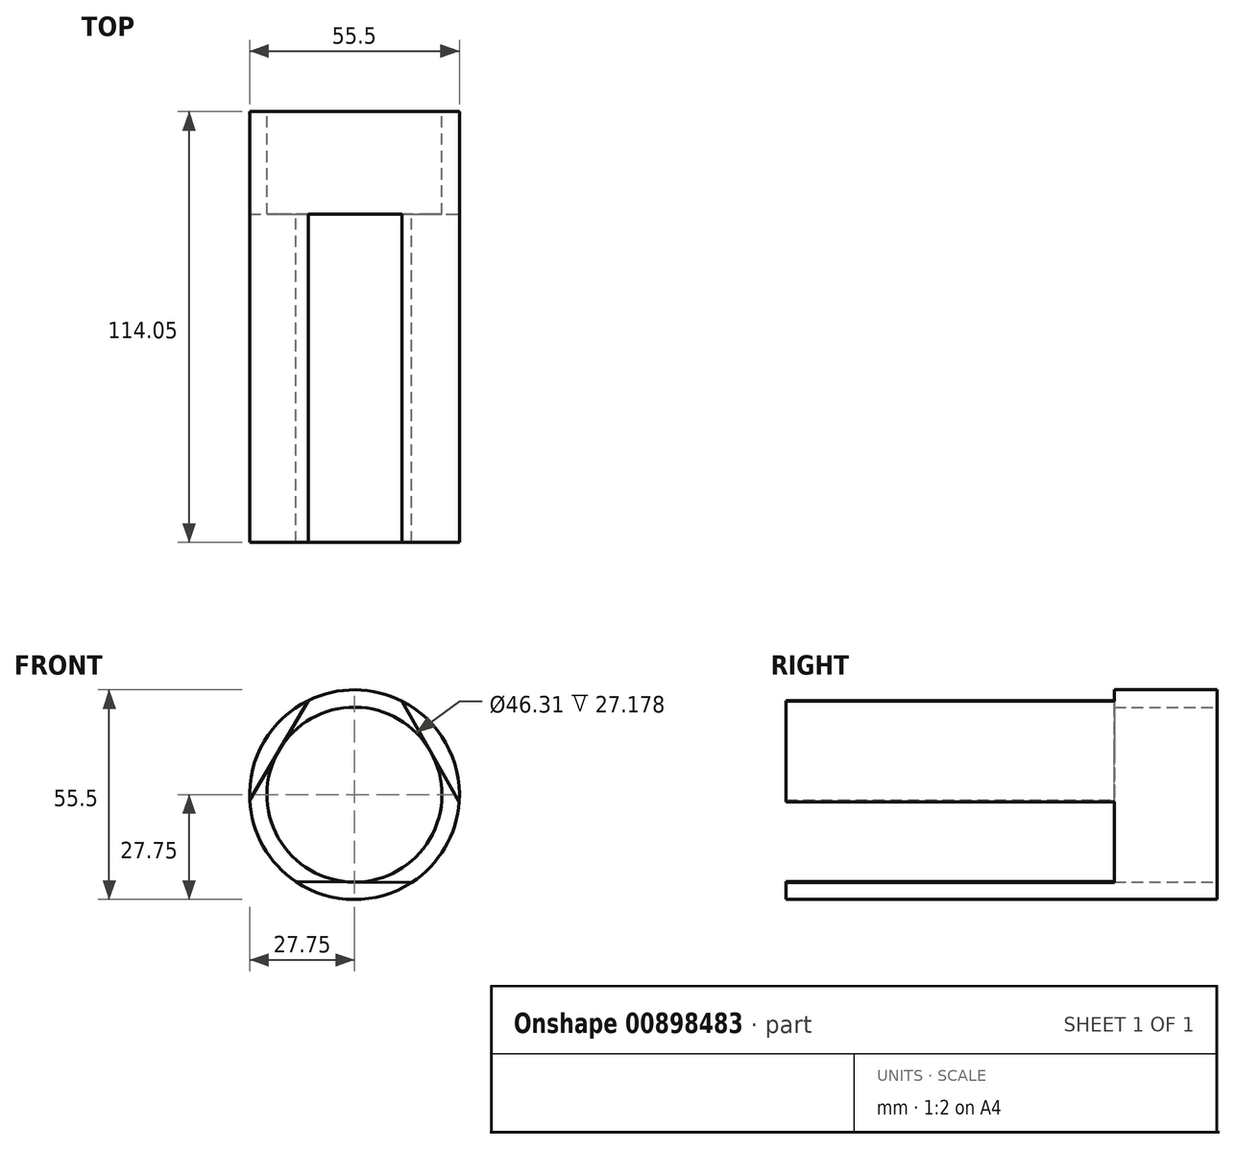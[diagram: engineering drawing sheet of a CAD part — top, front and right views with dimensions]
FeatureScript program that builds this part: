
annotation { "Feature Type Name" : "Feature", "Feature Type Description" : "" }
export const myFeature = defineFeature(function(context is Context, id is Id, definition is map)
    precondition{}
    {
        {
            var Q0;
            Q0=qCreatedBy(makeId("Front.planeOp"),FACE);
            var sketch = newSketch(context, id + "F0", { "sketchPlane" : qUnion([Q0])});
            skCircle(sketch, "E0", {"center": v(0, 0) * mm, "radius": 27.75 * mm});
            skCircle(sketch, "E1", {"center": v(0, 0) * mm, "radius": 23.15 * mm});
            skSolve(sketch);
        }
        {
            var Q0;
            Q0=makeQuery(id+"F0.imprint","IMPRINT",FACE,{"disambiguationData":[TD([[makeQuery(id+"F0.imprint","IMPRINT",EDGE,{"derivedFrom":sQuery(id+"F0.wireOp",EDGE,"E0")}),1.0]])]});
            extrude(context, id + "F1", {"entities" : qUnion([Q0]), "depth" : 114.05 * mm, "offsetDistance" : 25.4 * mm});
        }
        {
            var Q0;
            Q0=makeQuery(id+"F1.opExtrude","CAP_FACE",FACE,{"disambiguationData":[OSD([sQuery(id+"F0.wireOp",EDGE,"E0"),sQuery(id+"F0.wireOp",EDGE,"E1")])],"isStart":false});
            var sketch = newSketch(context, id + "F2", { "sketchPlane" : qUnion([Q0])});
            skCircle(sketch, "E2.cCircle", {"center": v(0, 0) * mm, "radius": 23.15 * mm, "construction": true});
            skLineSegment(sketch, "E2.0", {"start": v(0.36, 46.3) * mm, "end": v(39.92, -23.47) * mm});
            skLineSegment(sketch, "E2.1", {"start": v(39.92, -23.47) * mm, "end": v(-40.28, -22.84) * mm});
            skLineSegment(sketch, "E2.2", {"start": v(-40.28, -22.84) * mm, "end": v(0.36, 46.3) * mm});
            skPoint(sketch, "E2.0.midPoint", {"position": v(20.14, 11.42) * mm});
            skSolve(sketch);
        }
        {
            var Q0;
            Q0 = qSketchRegion(id + "F2", true);
            extrude(context, id + "F3", {"entities" : qUnion([Q0]), "operationType" : NewBodyOperationType.REMOVE, "oppositeDirection" : true, "depth" : 86.87 * mm, "offsetDistance" : 25.4 * mm});
        }
    });
